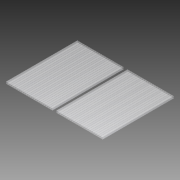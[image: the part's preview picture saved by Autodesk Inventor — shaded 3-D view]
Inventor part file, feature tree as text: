
AUTODESK INVENTOR PART (.ipt)
format: ipt  version: 2012 (Build 160160000, 160)  size: 286,208 bytes
history: native  units: in
note: dims shown in document units (in); Inventor stores cm internally (conversion verified against a paired STEP export)
features: extrude x1, sketch x1
ambient origin geometry x8: Origin, YZ Plane, XZ Plane, XY Plane, X Axis, Y Axis, Z Axis, Center Point
bodies: Solid1 (feature_tree)
feature tree (2):
  extrude  "Extrusion1"  Depth=0.25in
  sketch  "Sketch1"  dims[d0=12.02in d1=0.25in d2=0.0201in d3=0.02in d4=0.02in d5=0.23in d6=18.8976in d8=0.25in d9=0.3937in d11=1.0in d13=8.875in d14=0.0in]
